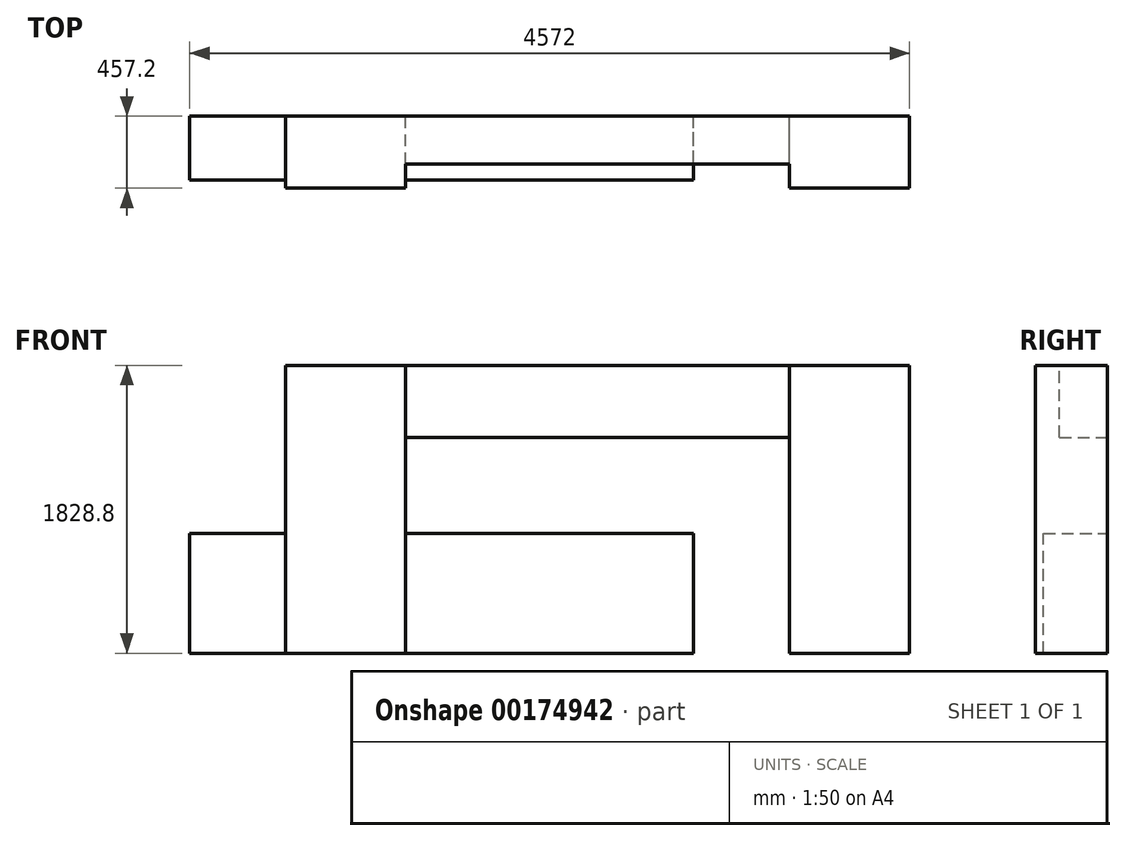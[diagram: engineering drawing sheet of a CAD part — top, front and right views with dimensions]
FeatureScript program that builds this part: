
annotation { "Feature Type Name" : "Feature", "Feature Type Description" : "" }
export const myFeature = defineFeature(function(context is Context, id is Id, definition is map)
    precondition{}
    {
        {
            var Q0;
            Q0=qCreatedBy(makeId("Front.planeOp"),FACE);
            var sketch = newSketch(context, id + "F0", { "sketchPlane" : qUnion([Q0])});
            skLineSegment(sketch, "E0.bottom", {"start": v(914.4, -381) * mm, "end": v(-914.4, -381) * mm});
            skLineSegment(sketch, "E0.top", {"start": v(914.4, 381) * mm, "end": v(-914.4, 381) * mm});
            skLineSegment(sketch, "E0.left", {"start": v(914.4, -381) * mm, "end": v(914.4, 381) * mm});
            skLineSegment(sketch, "E0.right", {"start": v(-914.4, -381) * mm, "end": v(-914.4, 381) * mm});
            skPoint(sketch, "E0.middle", {"position": v(0, 0) * mm});
            skLineSegment(sketch, "E1", {"start": v(-914.4, -584.2) * mm, "end": v(914.4, -584.2) * mm});
            skLineSegment(sketch, "E2", {"start": v(304.8, 381) * mm, "end": v(304.8, -381) * mm});
            skLineSegment(sketch, "E3", {"start": v(-304.8, 381) * mm, "end": v(-304.8, -381) * mm});
            skLineSegment(sketch, "E4.bottom", {"start": v(914.4, -381) * mm, "end": v(1524, -381) * mm});
            skLineSegment(sketch, "E4.top", {"start": v(914.4, 381) * mm, "end": v(1524, 381) * mm});
            skLineSegment(sketch, "E4.right", {"start": v(1524, -381) * mm, "end": v(1524, 381) * mm});
            skLineSegment(sketch, "E5.bottom", {"start": v(1524, -381) * mm, "end": v(2286, -381) * mm});
            skLineSegment(sketch, "E5.top", {"start": v(1524, 1447.8) * mm, "end": v(2286, 1447.8) * mm});
            skLineSegment(sketch, "E5.left", {"start": v(1524, -381) * mm, "end": v(1524, 1447.8) * mm});
            skLineSegment(sketch, "E5.right", {"start": v(2286, -381) * mm, "end": v(2286, 1447.8) * mm});
            skLineSegment(sketch, "E6.bottom", {"start": v(-914.4, -381) * mm, "end": v(-1676.4, -381) * mm});
            skLineSegment(sketch, "E6.top", {"start": v(-914.4, 1447.8) * mm, "end": v(-1676.4, 1447.8) * mm});
            skLineSegment(sketch, "E6.left", {"start": v(-914.4, -381) * mm, "end": v(-914.4, 1447.8) * mm});
            skLineSegment(sketch, "E6.right", {"start": v(-1676.4, -381) * mm, "end": v(-1676.4, 1447.8) * mm});
            skLineSegment(sketch, "E7.bottom", {"start": v(-1676.4, -381) * mm, "end": v(-2286, -381) * mm});
            skLineSegment(sketch, "E7.top", {"start": v(-1676.4, 381) * mm, "end": v(-2286, 381) * mm});
            skLineSegment(sketch, "E7.left", {"start": v(-1676.4, -381) * mm, "end": v(-1676.4, 381) * mm});
            skLineSegment(sketch, "E7.right", {"start": v(-2286, -381) * mm, "end": v(-2286, 381) * mm});
            skLineSegment(sketch, "E8.bottom", {"start": v(-914.4, 1447.8) * mm, "end": v(1524, 1447.8) * mm});
            skLineSegment(sketch, "E8.top", {"start": v(-914.4, 990.6) * mm, "end": v(1524, 990.6) * mm});
            skLineSegment(sketch, "E8.left", {"start": v(-914.4, 1447.8) * mm, "end": v(-914.4, 990.6) * mm});
            skLineSegment(sketch, "E8.right", {"start": v(1524, 1447.8) * mm, "end": v(1524, 990.6) * mm});
            skSolve(sketch);
        }
        {
            var Q0;
            {var subQ2=sQuery(id+"F0.wireOp",EDGE,"E0.right");Q0=makeQuery(id+"F0.imprint","IMPRINT",FACE,{"disambiguationData":[TD([[makeQuery(id+"F0.imprint","IMPRINT",EDGE,{"derivedFrom":subQ2}),-1.0]])]});}
            var Q1;
            {var subQ2=sQuery(id+"F0.wireOp",EDGE,"E2");Q1=makeQuery(id+"F0.imprint","IMPRINT",FACE,{"disambiguationData":[TD([[makeQuery(id+"F0.imprint","IMPRINT",EDGE,{"derivedFrom":subQ2}),-1.0]])]});}
            var Q2;
            {var subQ2=sQuery(id+"F0.wireOp",EDGE,"E0.left");Q2=makeQuery(id+"F0.imprint","IMPRINT",FACE,{"disambiguationData":[TD([[makeQuery(id+"F0.imprint","IMPRINT",EDGE,{"derivedFrom":subQ2}),1.0]])]});}
            var Q3;
            {var subQ0=sQuery(id+"F0.wireOp",EDGE,"E7.bottom");Q3=makeQuery(id+"F0.imprint","IMPRINT",FACE,{"disambiguationData":[TD([[makeQuery(id+"F0.imprint","IMPRINT",EDGE,{"derivedFrom":subQ0}),-1.0]])]});}
            extrude(context, id + "F1", {"entities" : qUnion([Q0, Q1, Q2, Q3]), "depth" : 406.4 * mm, "offsetDistance" : 25.4 * mm});
        }
        {
            var Q0;
            {var subQ1=sQuery(id+"F0.wireOp",EDGE,"E0.right");Q0=makeQuery(id+"F0.imprint","IMPRINT",FACE,{"disambiguationData":[TD([[makeQuery(id+"F0.imprint","IMPRINT",EDGE,{"derivedFrom":subQ1}),1.0]])]});}
            var Q1;
            {var subQ1=sQuery(id+"F0.wireOp",EDGE,"E4.right");Q1=makeQuery(id+"F0.imprint","IMPRINT",FACE,{"disambiguationData":[TD([[makeQuery(id+"F0.imprint","IMPRINT",EDGE,{"derivedFrom":subQ1}),-1.0]])]});}
            extrude(context, id + "F2", {"entities" : qUnion([Q0, Q1]), "operationType" : NewBodyOperationType.ADD, "depth" : 457.2 * mm, "offsetDistance" : 25.4 * mm});
        }
        {
            var Q0;
            {var subQ0=sQuery(id+"F0.wireOp",EDGE,"E8.bottom");Q0=makeQuery(id+"F0.imprint","IMPRINT",FACE,{"disambiguationData":[TD([[makeQuery(id+"F0.imprint","IMPRINT",EDGE,{"derivedFrom":subQ0}),-1.0]])]});}
            extrude(context, id + "F3", {"entities" : qUnion([Q0]), "operationType" : NewBodyOperationType.ADD, "depth" : 304.8 * mm, "offsetDistance" : 25.4 * mm});
        }
    });
